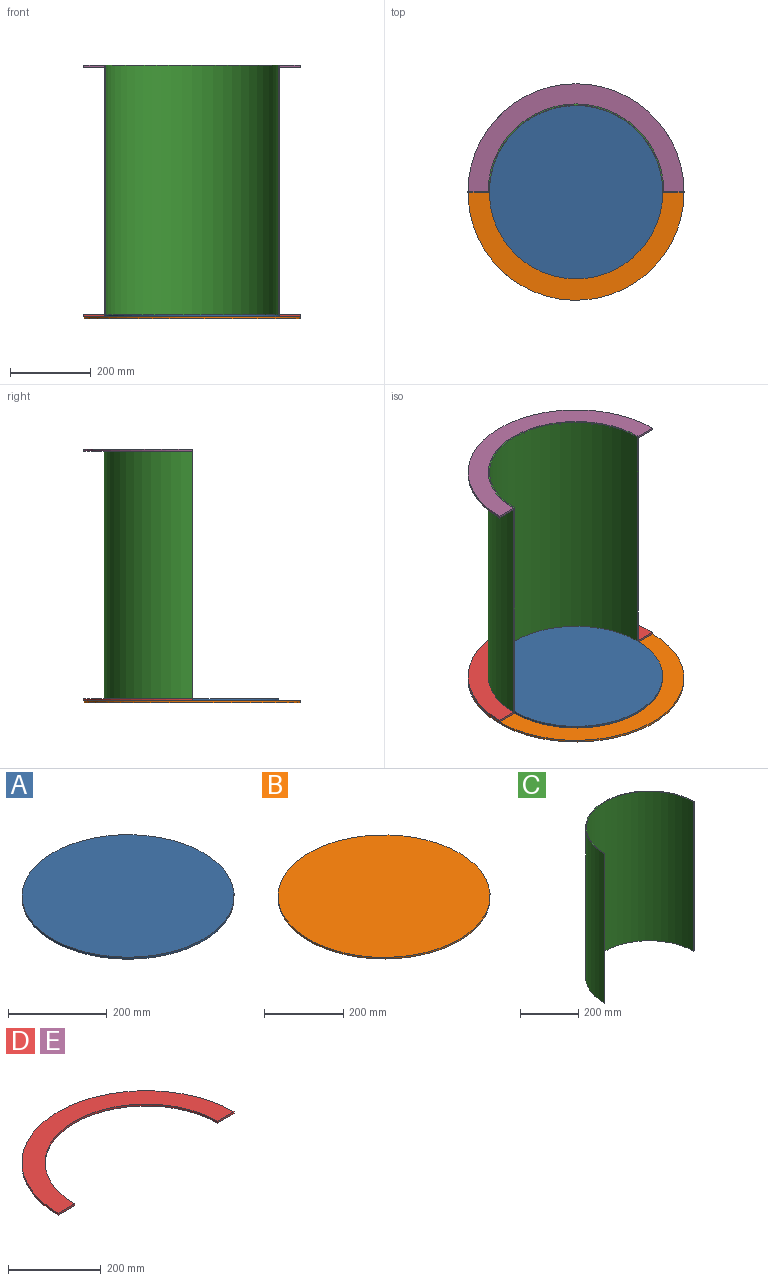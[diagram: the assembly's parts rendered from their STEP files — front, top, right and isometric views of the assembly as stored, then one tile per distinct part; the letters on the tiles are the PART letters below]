
ASSEMBLY  parts=5 mates=3
PART A: 3 faces, bbox 430x430x5 mm
  f0: cylinder r=215mm len=430mm, axis (0,0,-1), area 6754.4mm2, adj f1,f2
  f1: plane 430x430mm, normal (0,0,1), area 145220.1mm2, adj f0
  f2: plane 430x430mm, normal (0,0,-1), area 145220.1mm2, adj f0
PART B: 3 faces, bbox 536x536x5 mm
  f0: cylinder r=268mm len=536mm, axis (0,0,-1), area 8419.5mm2, adj f1,f2
  f1: plane 536x536mm, normal (0,0,1), area 225641.8mm2, adj f0
  f2: plane 536x536mm, normal (0,0,-1), area 225641.8mm2, adj f0
PART C: 6 faces, bbox 436x218x625 mm
  f0: cylinder r=215mm len=625mm, axis (0,0,-1), area 422151.5mm2, adj f1,f3,f4,f5
  f1: plane 625x3mm, normal (0,-1,0), area 1875mm2, adj f0,f2,f4,f5
  f2: cylinder r=218mm len=625mm, axis (0,0,-1), area 428042mm2, adj f1,f3,f4,f5
  f3: plane 625x3mm, normal (0,-1,0), area 1875mm2, adj f0,f2,f4,f5
  f4: plane 436x218mm, normal (0,0,1), area 2040.5mm2, adj f0,f1,f2,f3
  f5: plane 436x218mm, normal (0,0,-1), area 2040.5mm2, adj f0,f1,f2,f3
PART D: 6 faces, bbox 536x268x5 mm
  f0: cylinder r=218mm len=436mm, axis (0,0,-1), area 3424.3mm2, adj f1,f3,f4,f5
  f1: plane 50x5mm, normal (0,-1,0), area 250mm2, adj f0,f2,f4,f5
  f2: cylinder r=268mm len=536mm, axis (0,0,-1), area 4209.7mm2, adj f1,f3,f4,f5
  f3: plane 50x5mm, normal (0,-1,0), area 250mm2, adj f0,f2,f4,f5
  f4: plane 536x268mm, normal (0,0,1), area 38170.4mm2, adj f0,f1,f2,f3
  f5: plane 536x268mm, normal (0,0,-1), area 38170.4mm2, adj f0,f1,f2,f3
PART E: same geometry as D
PLACE A t=(48.96,115.93,-37.13)mm
PLACE B t=(48.96,115.93,-42.13)mm
PLACE C t=(48.96,115.93,-37.13)mm
PLACE D t=(48.96,115.93,-37.13)mm
PLACE E t=(48.96,115.93,582.87)mm
MATE fastened E.f4 <-> C.f4  axis (0,0,1) through (-169.04,115.93,587.87)mm
MATE fastened D.f5 <-> C.f5  axis (0,0,1) through (266.96,115.93,-37.13)mm
MATE planar A.f0 <-> B.f0  axis (0,0,-1) through (48.96,115.93,-37.13)mm
